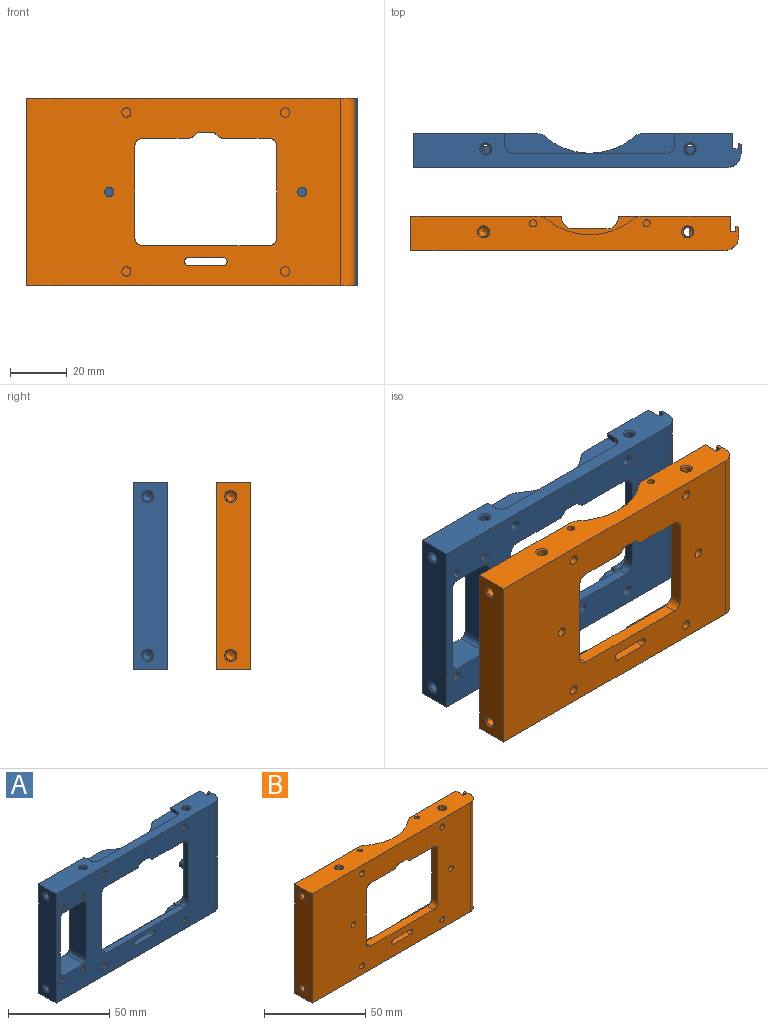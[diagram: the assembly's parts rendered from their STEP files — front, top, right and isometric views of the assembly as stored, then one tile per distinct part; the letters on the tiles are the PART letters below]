
ASSEMBLY  parts=2 mates=1
PART A: 149 faces, bbox 115.5x12x66 mm
  f0: plane 66x43.31mm, normal (0,1,0), area 1016.7mm2, adj f2,f12,f35,f41,f42,f43,f76,f77
  f1: plane 110.5x66mm, normal (0,-1,0), area 4002.6mm2, adj f2,f16,f17,f18,f19,f20,f21,f22
  f2: plane 115.5x12mm, normal (0,0,-1), area 945mm2, adj f0,f1,f5,f6,f13,f15,f40,f42
  f3: cylinder r=1.65mm len=9.5mm, axis (0,1,0), area 98.5mm2, adj f125,f141
  f4: cylinder r=1.65mm len=9.5mm, axis (0,1,0), area 98.5mm2, adj f128,f144
  f5: plane 7x5.5mm, normal (1,0,0), area 38.5mm2, adj f2,f9,f13,f128
  f6: plane 7x5.5mm, normal (-1,0,0), area 38.5mm2, adj f2,f10,f13,f125
  f7: cylinder r=3.5mm len=5.5mm, axis (0,-1,0), area 23.6mm2, adj f10,f11,f13,f125
  f8: cylinder r=3.5mm len=5.5mm, axis (0,-1,0), area 23.6mm2, adj f9,f13,f117,f128
  f9: cylinder r=5mm len=5.5mm, axis (0,1,0), area 11.8mm2, adj f5,f8,f13,f128
  f10: cylinder r=5mm len=5.5mm, axis (0,1,0), area 11.8mm2, adj f6,f7,f13,f125
  f11: cylinder r=5mm len=7.5mm, axis (0,-1,0), area 18.2mm2, adj f7,f13,f15,f78,f125,f126
  f12: plane 7.5x3.18mm, normal (0,0,1), area 21.8mm2, adj f0,f13,f52,f79,f117
  f13: plane 78x56.5mm, normal (0,1,0), area 1402.9mm2, adj f2,f5,f6,f7,f8,f9,f10,f11
  f14: plane 43.5x7.5mm, normal (-1,0,0), area 302.3mm2, adj f13,f15,f83,f84,f85,f89,f90
  f15: plane 66x31.41mm, normal (0,1,0), area 939.7mm2, adj f2,f11,f14,f34,f41,f44,f47,f74
  f16: plane 54.5x3.5mm, normal (0,0,1), area 190.7mm2, adj f1,f29,f30,f109
  f17: cylinder r=3mm len=3.5mm, axis (0,1,0), area 16.5mm2, adj f1,f18,f31,f115
  f18: plane 21.75x3.5mm, normal (0,0,-1), area 76.1mm2, adj f1,f17,f19,f116
  f19: cylinder r=1mm len=3.5mm, axis (0,1,0), area 2.6mm2, adj f1,f18,f20,f114
  f20: plane 3.5x1.63mm, normal (0.68,0,-0.73), area 7.8mm2, adj f1,f19,f21,f112
  f21: cylinder r=1.75mm len=3.5mm, axis (0,1,0), area 4.6mm2, adj f1,f20,f22,f110
  f22: plane 4x3.5mm, normal (0,0,-1), area 14mm2, adj f1,f21,f23,f108
  f23: cylinder r=1.75mm len=3.5mm, axis (0,1,0), area 4.6mm2, adj f1,f22,f24,f106
  f24: plane 3.5x1.63mm, normal (-0.68,0,-0.73), area 7.8mm2, adj f1,f23,f25,f104
  f25: cylinder r=1mm len=3.5mm, axis (0,1,0), area 2.6mm2, adj f1,f24,f26,f102
  f26: plane 21.75x3.5mm, normal (0,0,-1), area 76.1mm2, adj f1,f25,f27,f101
  f27: cylinder r=3mm len=3.5mm, axis (0,1,0), area 16.5mm2, adj f1,f26,f28,f103
  f28: plane 34.5x3.5mm, normal (-1,0,0), area 120.8mm2, adj f1,f27,f29,f105
  f29: cylinder r=3mm len=3.5mm, axis (0,1,0), area 16.5mm2, adj f1,f16,f28,f107
  f30: cylinder r=3mm len=3.5mm, axis (0,1,0), area 16.5mm2, adj f1,f16,f31,f111
  f31: plane 34.5x3.5mm, normal (1,0,0), area 120.8mm2, adj f1,f17,f30,f113
  f32: cylinder r=1.65mm len=9.15mm, axis (0,0,1), area 93.6mm2, adj f59,f82,f83
  f33: cylinder r=24mm len=31.27mm, axis (0,0,1), area 253.4mm2, adj f34,f35,f45,f82,f121,f124
  f34: cylinder r=5mm len=7.5mm, axis (0,0,1), area 26.6mm2, adj f15,f33,f82,f121
  f35: cylinder r=5mm len=7.5mm, axis (0,0,1), area 26.6mm2, adj f0,f33,f82,f124
  f36: cylinder r=1.5mm len=4.5mm, axis (0,1,0), area 21.2mm2, adj f1,f13,f37,f39
  f37: plane 12x4.5mm, normal (0,0,-1), area 54mm2, adj f1,f13,f36,f38
  f38: cylinder r=1.5mm len=4.5mm, axis (0,1,0), area 21.2mm2, adj f1,f13,f37,f39
  f39: plane 12x4.5mm, normal (0,0,1), area 54mm2, adj f1,f13,f36,f38
  f40: plane 66x3mm, normal (1,0,0), area 198mm2, adj f2,f41,f46,f51
  f41: plane 115.5x12mm, normal (0,0,1), area 920.8mm2, adj f0,f1,f15,f40,f42,f46,f47,f48
  f42: plane 66x12mm, normal (-1,0,0), area 763mm2, adj f0,f1,f2,f41,f64,f65
  f43: cylinder r=1.65mm len=11.5mm, axis (0,1,0), area 119.2mm2, adj f0,f143
  f44: cylinder r=1.65mm len=11.5mm, axis (0,1,0), area 119.2mm2, adj f15,f142
  f45: cylinder r=0.8mm len=5mm, axis (0,1,0), area 25.1mm2, adj f1,f33
  f46: cylinder r=5mm len=66mm, axis (0,0,-1), area 518.4mm2, adj f1,f2,f40,f41
  f47: plane 66x5.5mm, normal (1,0,0), area 363mm2, adj f2,f15,f41,f48
  f48: plane 66x2mm, normal (0,1,0), area 132mm2, adj f2,f41,f47,f49
  f49: plane 66x2mm, normal (-1,0,0), area 132mm2, adj f2,f41,f48,f50
  f50: plane 66x0.5mm, normal (0,1,0), area 33mm2, adj f2,f41,f49,f51
  f51: plane 66x0.5mm, normal (0.71,0.71,0), area 46.7mm2, adj f2,f40,f41,f50
  f52: cylinder r=1.65mm len=7.64mm, axis (0,0,-1), area 70.8mm2, adj f12,f55,f79
  f53: cylinder r=1.65mm len=6.65mm, axis (0,0,-1), area 67.7mm2, adj f54,f78,f84
  f54: cone r=1.65mm half-angle=45deg, axis (0,0,-1), area 8.4mm2, adj f2,f53
  f55: cone r=1.65mm half-angle=45deg, axis (0,0,-1), area 8.4mm2, adj f2,f52
  f56: cone r=0mm half-angle=59deg, axis (0,0,1), area 0.9mm2, adj f57,f81
  f57: cylinder r=1.65mm len=9.5mm, axis (0,0,1), area 95.5mm2, adj f56,f58,f81,f82
  f58: cone r=1.65mm half-angle=45deg, axis (0,0,1), area 8.4mm2, adj f41,f57
  f59: cone r=1.65mm half-angle=45deg, axis (0,0,1), area 8.4mm2, adj f32,f41
  f60: cone r=0mm half-angle=59deg, axis (-1,0,0), area 10mm2, adj f61
  f61: cylinder r=1.65mm len=11.6mm, axis (-1,0,0), area 120.3mm2, adj f60,f65
  f62: cone r=0mm half-angle=59deg, axis (-1,0,0), area 10mm2, adj f63
  f63: cylinder r=1.65mm len=11.6mm, axis (-1,0,0), area 120.3mm2, adj f62,f64
  f64: cone r=1.65mm half-angle=45deg, axis (-1,0,0), area 8.4mm2, adj f42,f63
  f65: cone r=1.65mm half-angle=45deg, axis (-1,0,0), area 8.4mm2, adj f42,f61
  f66: cone r=0mm half-angle=59deg, axis (0,1,0), area 5.7mm2, adj f67
  f67: cylinder r=1.25mm len=8mm, axis (0,1,0), area 62.8mm2, adj f66,f77
  f68: cone r=0mm half-angle=59deg, axis (0,1,0), area 5.7mm2, adj f69
  f69: cylinder r=1.25mm len=8mm, axis (0,1,0), area 62.8mm2, adj f68,f76
  f70: cone r=0mm half-angle=59deg, axis (0,1,0), area 5.7mm2, adj f71
  f71: cylinder r=1.25mm len=8mm, axis (0,1,0), area 62.8mm2, adj f70,f75
  f72: cone r=0mm half-angle=59deg, axis (0,1,0), area 5.7mm2, adj f73
  f73: cylinder r=1.25mm len=8mm, axis (0,1,0), area 62.8mm2, adj f72,f74
  f74: cone r=1.25mm half-angle=45deg, axis (0,1,0), area 6.7mm2, adj f15,f73
  f75: cone r=1.25mm half-angle=45deg, axis (0,1,0), area 6.7mm2, adj f15,f71
  f76: cone r=1.25mm half-angle=45deg, axis (0,1,0), area 6.7mm2, adj f0,f69
  f77: cone r=1.25mm half-angle=45deg, axis (0,1,0), area 6.7mm2, adj f0,f67
  f78: plane 7.5x3.18mm, normal (0,0,1), area 17.3mm2, adj f11,f13,f15,f53,f84
  f79: cylinder r=3mm len=7.5mm, axis (0,1,0), area 28.1mm2, adj f0,f12,f13,f52,f80
  f80: plane 43.5x7.5mm, normal (1,0,0), area 302.3mm2, adj f0,f13,f79,f81,f92,f93,f96
  f81: cylinder r=3mm len=7.5mm, axis (0,1,0), area 29.1mm2, adj f0,f13,f56,f57,f80,f82
  f82: plane 72x7.5mm, normal (0,0,-1), area 367.2mm2, adj f0,f13,f15,f32,f33,f34,f35,f57
  f83: cylinder r=3mm len=7.5mm, axis (0,1,0), area 33.3mm2, adj f13,f14,f15,f32,f82
  f84: cylinder r=3mm len=7.5mm, axis (0,1,0), area 33.3mm2, adj f13,f14,f15,f53,f78
  f85: cylinder r=2mm len=3mm, axis (0,-1,0), area 9.4mm2, adj f13,f14,f86,f90
  f86: plane 3x3mm, normal (0,0,-1), area 9mm2, adj f13,f85,f87,f90
  f87: cylinder r=2.38mm len=4.75mm, axis (0,-1,0), area 22.4mm2, adj f13,f86,f88,f90
  f88: plane 3x2.99mm, normal (0,0,1), area 9mm2, adj f13,f87,f89,f90
  f89: cylinder r=2.25mm len=3mm, axis (0,-1,0), area 7.5mm2, adj f13,f14,f88,f90
  f90: plane 8x7.38mm, normal (0,1,0), area 29.3mm2, adj f14,f85,f86,f87,f88,f89,f100
  f91: plane 3x3mm, normal (0,0,-1), area 9mm2, adj f13,f92,f95,f96
  f92: cylinder r=2mm len=3mm, axis (0,-1,0), area 9.4mm2, adj f13,f80,f91,f96
  f93: cylinder r=2.25mm len=3mm, axis (0,-1,0), area 7.5mm2, adj f13,f80,f94,f96
  f94: plane 3x2.99mm, normal (0,0,1), area 9mm2, adj f13,f93,f95,f96
  f95: cylinder r=2.38mm len=4.75mm, axis (0,-1,0), area 22.4mm2, adj f13,f91,f94,f96
  f96: plane 8x7.38mm, normal (0,1,0), area 29.3mm2, adj f80,f91,f92,f93,f94,f95,f98
  f97: cone r=0mm half-angle=59deg, axis (0,1,0), area 5.7mm2, adj f98
  f98: cylinder r=1.25mm len=5.5mm, axis (0,1,0), area 43.2mm2, adj f96,f97
  f99: cone r=0mm half-angle=59deg, axis (0,1,0), area 5.7mm2, adj f100
  f100: cylinder r=1.25mm len=5.5mm, axis (0,1,0), area 43.2mm2, adj f90,f99
  f101: plane 21.75x1mm, normal (0,0.71,-0.71), area 30.8mm2, adj f13,f26,f102,f103
  f102: cone r=1mm half-angle=45deg, axis (0,-1,0), area 0.5mm2, adj f25,f101,f104
  f103: cone r=3mm half-angle=45deg, axis (0,1,0), area 7.8mm2, adj f13,f27,f101,f105
  f104: plane 2.31x2.25mm, normal (-0.48,0.71,-0.52), area 3.1mm2, adj f13,f24,f102,f106
  f105: plane 34.5x1mm, normal (-0.71,0.71,0), area 48.8mm2, adj f13,f28,f103,f107
  f106: cone r=1.75mm half-angle=45deg, axis (0,1,0), area 2.4mm2, adj f13,f23,f104,f108
  f107: cone r=3mm half-angle=45deg, axis (0,1,0), area 7.8mm2, adj f13,f29,f105,f109
  f108: plane 4x1mm, normal (0,0.71,-0.71), area 5.7mm2, adj f22,f82,f106,f110
  f109: plane 54.5x1mm, normal (0,0.71,0.71), area 77.1mm2, adj f13,f16,f107,f111
  f110: cone r=2.75mm half-angle=45deg, axis (0,1,0), area 2.4mm2, adj f13,f21,f108,f112
  f111: cone r=3mm half-angle=45deg, axis (0,1,0), area 7.8mm2, adj f13,f30,f109,f113
  f112: plane 2.31x2.25mm, normal (0.48,0.71,-0.52), area 3.1mm2, adj f13,f20,f110,f114
  f113: plane 34.5x1mm, normal (0.71,0.71,0), area 48.8mm2, adj f13,f31,f111,f115
  f114: cone r=1mm half-angle=45deg, axis (0,-1,0), area 0.5mm2, adj f19,f112,f116
  f115: cone r=3mm half-angle=45deg, axis (0,1,0), area 7.8mm2, adj f13,f17,f113,f116
  f116: plane 21.75x1mm, normal (0,0.71,-0.71), area 30.8mm2, adj f13,f18,f114,f115
  f117: cylinder r=5mm len=7.5mm, axis (0,-1,0), area 18.2mm2, adj f0,f8,f12,f13,f127,f128
  f118: plane 54x2mm, normal (0,1,0), area 108mm2, adj f41,f119,f121,f123,f124
  f119: cylinder r=3mm len=3mm, axis (0,0,1), area 9.4mm2, adj f41,f118,f120,f121
  f120: plane 4x2mm, normal (-1,0,0), area 8mm2, adj f15,f41,f119,f121
  f121: plane 30x7mm, normal (0,0,1), area 125.9mm2, adj f15,f33,f34,f118,f119,f120
  f122: plane 4x2mm, normal (1,0,0), area 8mm2, adj f0,f41,f123,f124
  f123: cylinder r=3mm len=3mm, axis (0,0,1), area 9.4mm2, adj f41,f118,f122,f124
  f124: plane 30x7mm, normal (0,0,1), area 125.9mm2, adj f0,f33,f35,f118,f122,f123
  f125: plane 8.5x8mm, normal (0,1,0), area 54.1mm2, adj f2,f3,f6,f7,f10,f11,f126
  f126: plane 7.07x2mm, normal (-1,0,0), area 14.1mm2, adj f2,f11,f15,f125
  f127: plane 7.07x2mm, normal (1,0,0), area 14.1mm2, adj f0,f2,f117,f128
  f128: plane 8.5x8mm, normal (0,1,0), area 54.1mm2, adj f2,f4,f5,f8,f9,f117,f127
  f129: plane 34.03x12mm, normal (1,0,0), area 408.4mm2, adj f0,f1,f130,f136
  f130: cylinder r=2mm len=12mm, axis (0,1,0), area 37.7mm2, adj f0,f1,f129,f131
  f131: plane 14.2x12mm, normal (0,0,-1), area 170.4mm2, adj f0,f1,f130,f132
  f132: cylinder r=2mm len=12mm, axis (0,1,0), area 37.7mm2, adj f0,f1,f131,f133
  f133: plane 34.03x12mm, normal (-1,0,0), area 408.4mm2, adj f0,f1,f132,f134
  f134: cylinder r=2mm len=12mm, axis (0,1,0), area 37.7mm2, adj f0,f1,f133,f135
  f135: plane 14.2x12mm, normal (0,0,1), area 170.4mm2, adj f0,f1,f134,f136
  f136: cylinder r=2mm len=12mm, axis (0,1,0), area 37.7mm2, adj f0,f1,f129,f135
  f137: cylinder r=1.25mm len=11.5mm, axis (0,-1,0), area 90.3mm2, adj f0,f146
  f138: cylinder r=1.25mm len=11.5mm, axis (0,-1,0), area 90.3mm2, adj f0,f145
  f139: cylinder r=1.25mm len=11.5mm, axis (0,-1,0), area 90.3mm2, adj f0,f147
  f140: cylinder r=1.25mm len=11.5mm, axis (0,-1,0), area 90.3mm2, adj f0,f148
  f141: cone r=1.65mm half-angle=45deg, axis (0,-1,0), area 8.4mm2, adj f1,f3
  f142: cone r=2.15mm half-angle=45deg, axis (0,-1,0), area 8.4mm2, adj f1,f44
  f143: cone r=1.65mm half-angle=45deg, axis (0,-1,0), area 8.4mm2, adj f1,f43
  f144: cone r=2.15mm half-angle=45deg, axis (0,-1,0), area 8.4mm2, adj f1,f4
  f145: cone r=1.25mm half-angle=45deg, axis (0,-1,0), area 6.7mm2, adj f1,f138
  f146: cone r=1.25mm half-angle=45deg, axis (0,-1,0), area 6.7mm2, adj f1,f137
  f147: cone r=1.25mm half-angle=45deg, axis (0,-1,0), area 6.7mm2, adj f1,f139
  f148: cone r=1.25mm half-angle=45deg, axis (0,-1,0), area 6.7mm2, adj f1,f140
PART B: 99 faces, bbox 115.5x12x66 mm
  f0: plane 16.17x4.5mm, normal (0,0,-1), area 72.8mm2, adj f1,f8,f28,f92
  f1: plane 110.5x66mm, normal (0,-1,0), area 5290.3mm2, adj f0,f3,f4,f12,f13,f14,f16,f17
  f2: plane 66x53mm, normal (0,1,0), area 1897.5mm2, adj f3,f4,f9,f10,f21,f37,f44,f45
  f3: plane 70x12mm, normal (0,0,1), area 494mm2, adj f1,f2,f5,f6,f8,f12,f14,f50
  f4: plane 115.5x12mm, normal (0,0,1), area 1179.7mm2, adj f1,f2,f5,f11,f15,f31,f32,f33
  f5: plane 66x39.5mm, normal (0,1,0), area 1006.5mm2, adj f3,f4,f6,f7,f21,f32,f39,f40
  f6: plane 7.5x6mm, normal (-1,0,0), area 34.3mm2, adj f3,f5,f8,f41,f60,f61
  f7: plane 7.5x6mm, normal (-1,0,0), area 34.3mm2, adj f5,f8,f39,f48,f54,f55
  f8: plane 80x52mm, normal (0,1,0), area 2057.8mm2, adj f0,f3,f6,f7,f9,f10,f12,f13
  f9: plane 7.5x1mm, normal (0,0,1), area 7.5mm2, adj f2,f8,f44,f50
  f10: plane 7.5x1mm, normal (0,0,-1), area 7.5mm2, adj f2,f8,f45,f49
  f11: plane 66x0.5mm, normal (0,1,0), area 33mm2, adj f4,f21,f34,f35
  f12: cylinder r=1.5mm len=4.5mm, axis (0,1,0), area 21.2mm2, adj f1,f3,f8,f13
  f13: plane 12x4.5mm, normal (0,0,-1), area 54mm2, adj f1,f8,f12,f14
  f14: cylinder r=1.5mm len=4.5mm, axis (0,1,0), area 21.2mm2, adj f1,f3,f8,f13
  f15: plane 66x3mm, normal (1,0,0), area 198mm2, adj f4,f21,f31,f35
  f16: plane 44x4.5mm, normal (0,0,1), area 198mm2, adj f1,f8,f27,f30
  f17: plane 32x4.5mm, normal (1,0,0), area 144mm2, adj f1,f8,f27,f28
  f18: plane 16.17x4.5mm, normal (0,0,-1), area 72.8mm2, adj f1,f8,f29,f98
  f19: cylinder r=1.65mm len=4.5mm, axis (0,1,0), area 46.7mm2, adj f1,f8
  f20: cylinder r=1.65mm len=4.5mm, axis (0,1,0), area 46.7mm2, adj f1,f8
  f21: plane 115.5x12mm, normal (0,0,-1), area 1257.8mm2, adj f1,f2,f5,f11,f15,f31,f32,f33
  f22: plane 32x4.5mm, normal (-1,0,0), area 144mm2, adj f1,f8,f29,f30
  f23: cylinder r=1.65mm len=4.5mm, axis (0,1,0), area 46.7mm2, adj f1,f36
  f24: cylinder r=1.65mm len=4.5mm, axis (0,1,0), area 46.7mm2, adj f1,f42
  f25: cylinder r=1.65mm len=4.5mm, axis (0,1,0), area 46.7mm2, adj f1,f43
  f26: cylinder r=1.65mm len=4.5mm, axis (0,1,0), area 46.7mm2, adj f1,f38
  f27: cylinder r=3mm len=4.5mm, axis (0,-1,0), area 21.2mm2, adj f1,f8,f16,f17
  f28: cylinder r=3mm len=4.5mm, axis (0,1,0), area 21.2mm2, adj f0,f1,f8,f17
  f29: cylinder r=3mm len=4.5mm, axis (0,-1,0), area 21.2mm2, adj f1,f8,f18,f22
  f30: cylinder r=3mm len=4.5mm, axis (0,1,0), area 21.2mm2, adj f1,f8,f16,f22
  f31: cylinder r=5mm len=66mm, axis (0,0,-1), area 518.4mm2, adj f1,f4,f15,f21
  f32: plane 66x5.5mm, normal (1,0,0), area 363mm2, adj f4,f5,f21,f33
  f33: plane 66x2mm, normal (0,1,0), area 132mm2, adj f4,f21,f32,f34
  f34: plane 66x2mm, normal (-1,0,0), area 132mm2, adj f4,f11,f21,f33
  f35: plane 66x0.5mm, normal (0.71,0.71,0), area 46.7mm2, adj f4,f11,f15,f21
  f36: plane 3.3x3.3mm, normal (0,-1,0), area 8.6mm2, adj f23
  f37: plane 32x7.5mm, normal (1,0,0), area 240mm2, adj f2,f8,f44,f45
  f38: plane 3.3x3.3mm, normal (0,-1,0), area 8.6mm2, adj f26
  f39: plane 7.5x1mm, normal (0,0,-1), area 7.5mm2, adj f5,f7,f8,f47
  f40: plane 32x7.5mm, normal (-1,0,0), area 240mm2, adj f5,f8,f46,f47
  f41: plane 7.5x1mm, normal (0,0,1), area 7.5mm2, adj f5,f6,f8,f46
  f42: plane 3.3x3.3mm, normal (0,-1,0), area 8.6mm2, adj f24
  f43: plane 3.3x3.3mm, normal (0,-1,0), area 8.6mm2, adj f25
  f44: cylinder r=4mm len=7.5mm, axis (0,-1,0), area 47.1mm2, adj f2,f8,f9,f37
  f45: cylinder r=4mm len=7.5mm, axis (0,-1,0), area 47.1mm2, adj f2,f8,f10,f37
  f46: cylinder r=4mm len=7.5mm, axis (0,-1,0), area 47.1mm2, adj f5,f8,f40,f41
  f47: cylinder r=4mm len=7.5mm, axis (0,-1,0), area 47.1mm2, adj f5,f8,f39,f40
  f48: plane 70x7.5mm, normal (0,0,-1), area 361.8mm2, adj f2,f5,f7,f8,f49,f51,f52,f53
  f49: plane 7.5x6mm, normal (1,0,0), area 45mm2, adj f2,f8,f10,f48
  f50: plane 7.5x6mm, normal (1,0,0), area 45mm2, adj f2,f3,f8,f9
  f51: cylinder r=24mm len=30.28mm, axis (0,0,1), area 229.4mm2, adj f4,f48,f66,f67
  f52: cylinder r=1.25mm len=7mm, axis (0,0,1), area 55mm2, adj f4,f48
  f53: cylinder r=1.25mm len=7mm, axis (0,0,1), area 55mm2, adj f4,f48
  f54: cone r=0mm half-angle=59deg, axis (0,0,1), area 3.1mm2, adj f7,f55
  f55: cylinder r=1.65mm len=9.5mm, axis (0,0,1), area 79.9mm2, adj f7,f48,f54,f59
  f56: cone r=0mm half-angle=59deg, axis (0,0,1), area 10mm2, adj f57
  f57: cylinder r=1.65mm len=9.5mm, axis (0,0,1), area 98.5mm2, adj f56,f58
  f58: cone r=1.65mm half-angle=45deg, axis (0,0,1), area 8.4mm2, adj f4,f57
  f59: cone r=1.65mm half-angle=45deg, axis (0,0,1), area 8.4mm2, adj f4,f55
  f60: cone r=0mm half-angle=59deg, axis (0,0,-1), area 3.1mm2, adj f6,f61
  f61: cylinder r=1.65mm len=9.5mm, axis (0,0,-1), area 79.9mm2, adj f3,f6,f60,f65
  f62: cone r=0mm half-angle=59deg, axis (0,0,-1), area 10mm2, adj f63
  f63: cylinder r=1.65mm len=9.5mm, axis (0,0,-1), area 98.5mm2, adj f62,f64
  f64: cone r=1.65mm half-angle=45deg, axis (0,0,-1), area 8.4mm2, adj f21,f63
  f65: cone r=1.65mm half-angle=45deg, axis (0,0,-1), area 8.4mm2, adj f21,f61
  f66: cylinder r=5mm len=7mm, axis (0,0,1), area 23.9mm2, adj f2,f4,f48,f51
  f67: cylinder r=5mm len=7mm, axis (0,0,1), area 23.9mm2, adj f4,f5,f48,f51
  f68: plane 66x12mm, normal (-1,0,0), area 763mm2, adj f1,f2,f4,f21,f73,f74
  f69: cone r=0mm half-angle=59deg, axis (-1,0,0), area 10mm2, adj f70
  f70: cylinder r=1.65mm len=9.5mm, axis (-1,0,0), area 98.5mm2, adj f69,f74
  f71: cone r=0mm half-angle=59deg, axis (-1,0,0), area 10mm2, adj f72
  f72: cylinder r=1.65mm len=9.5mm, axis (-1,0,0), area 98.5mm2, adj f71,f73
  f73: cone r=1.65mm half-angle=45deg, axis (-1,0,0), area 8.4mm2, adj f68,f72
  f74: cone r=1.65mm half-angle=45deg, axis (-1,0,0), area 8.4mm2, adj f68,f70
  f75: cone r=0mm half-angle=59deg, axis (0,1,0), area 19.4mm2, adj f76
  f76: cylinder r=2.3mm len=7.5mm, axis (0,1,0), area 108.4mm2, adj f75,f86
  f77: cone r=0mm half-angle=59deg, axis (0,1,0), area 19.4mm2, adj f78
  f78: cylinder r=2.3mm len=7.5mm, axis (0,1,0), area 108.4mm2, adj f77,f85
  f79: cone r=0mm half-angle=59deg, axis (0,1,0), area 19.4mm2, adj f80
  f80: cylinder r=2.3mm len=7.5mm, axis (0,1,0), area 108.4mm2, adj f79,f84
  f81: cone r=0mm half-angle=59deg, axis (0,1,0), area 19.4mm2, adj f82
  f82: cylinder r=2.3mm len=7.5mm, axis (0,1,0), area 108.4mm2, adj f81,f83
  f83: cone r=2.3mm half-angle=45deg, axis (0,1,0), area 11.3mm2, adj f5,f82
  f84: cone r=2.3mm half-angle=45deg, axis (0,1,0), area 11.3mm2, adj f5,f80
  f85: cone r=2.3mm half-angle=45deg, axis (0,1,0), area 11.3mm2, adj f2,f78
  f86: cone r=2.3mm half-angle=45deg, axis (0,1,0), area 11.3mm2, adj f2,f76
  f87: plane 7x0.3mm, normal (-1,0,0), area 2.1mm2, adj f3,f5,f21,f88
  f88: cylinder r=4mm len=7mm, axis (0,0,-1), area 44mm2, adj f3,f21,f87,f89
  f89: plane 12x7mm, normal (0,1,0), area 84mm2, adj f3,f21,f88,f90
  f90: cylinder r=4mm len=7mm, axis (0,0,-1), area 44mm2, adj f3,f21,f89,f91
  f91: plane 7x0.3mm, normal (1,0,0), area 2.1mm2, adj f2,f3,f21,f90
  f92: cylinder r=2mm len=4.5mm, axis (0,1,0), area 7.1mm2, adj f0,f1,f8,f93
  f93: plane 4.5x0.83mm, normal (0.71,0,-0.71), area 5.3mm2, adj f1,f8,f92,f94
  f94: cylinder r=2mm len=4.5mm, axis (0,1,0), area 7.1mm2, adj f1,f8,f93,f95
  f95: plane 4.5x4.34mm, normal (0,0,-1), area 19.5mm2, adj f1,f8,f94,f96
  f96: cylinder r=2mm len=4.5mm, axis (0,1,0), area 7.1mm2, adj f1,f8,f95,f97
  f97: plane 4.5x0.83mm, normal (-0.71,0,-0.71), area 5.3mm2, adj f1,f8,f96,f98
  f98: cylinder r=2mm len=4.5mm, axis (0,1,0), area 7.1mm2, adj f1,f8,f18,f97
PLACE A t=(13.14,30.89,-2.6)mm
PLACE B t=(13.14,-5.84,-2.6)mm
MATE planar B.f4 <-> A.f41  axis (0,0,1) through (6.14,-4.82,30.4)mm
